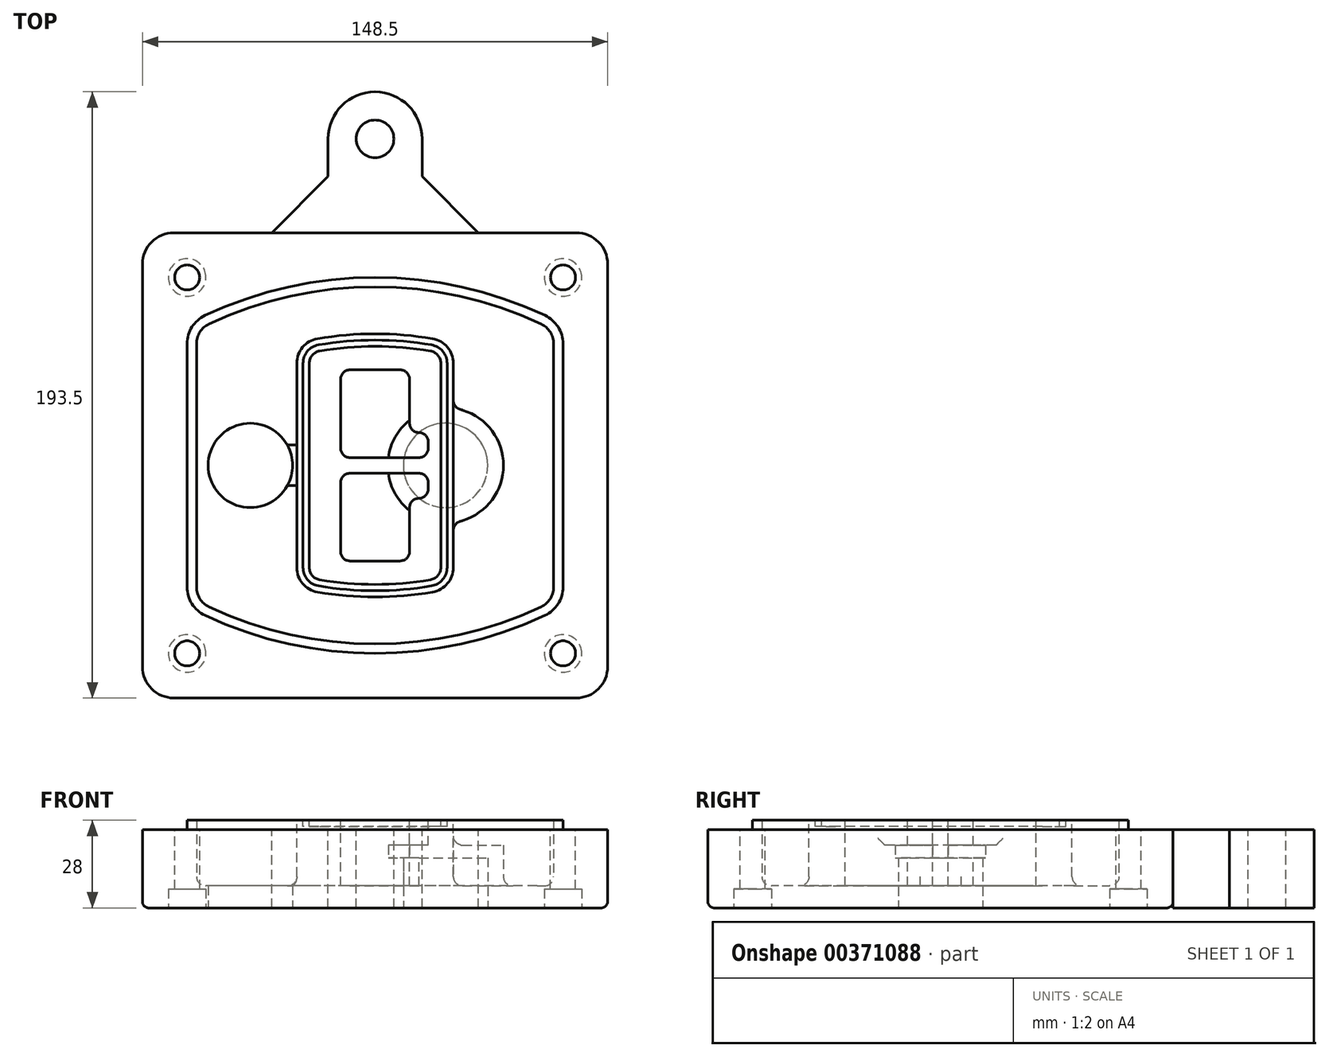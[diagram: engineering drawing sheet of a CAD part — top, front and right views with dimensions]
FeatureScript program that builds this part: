
annotation { "Feature Type Name" : "Feature", "Feature Type Description" : "" }
export const myFeature = defineFeature(function(context is Context, id is Id, definition is map)
    precondition{}
    {
        {
            var Q0;
            Q0=qCreatedBy(makeId("Top.planeOp"),FACE);
            var sketch = newSketch(context, id + "F0", { "sketchPlane" : qUnion([Q0])});
            skPoint(sketch, "E0.rect.middle", {"position": v(0, 0) * mm});
            skLineSegment(sketch, "E1.bottom", {"start": v(-64.25, -74.25) * mm, "end": v(64.25, -74.25) * mm});
            skLineSegment(sketch, "E1.top", {"start": v(-64.25, 74.25) * mm, "end": v(64.25, 74.25) * mm});
            skLineSegment(sketch, "E1.left", {"start": v(-74.25, -64.25) * mm, "end": v(-74.25, 64.25) * mm});
            skLineSegment(sketch, "E1.right", {"start": v(74.25, -64.25) * mm, "end": v(74.25, 64.25) * mm});
            skLineSegment(sketch, "E2", {"start": v(-74.25, 74.25) * mm, "end": v(74.25, -74.25) * mm, "construction": true});
            skLineSegment(sketch, "E3", {"start": v(74.25, 74.25) * mm, "end": v(-74.25, -74.25) * mm, "construction": true});
            skCircle(sketch, "E4", {"center": v(-60, 60) * mm, "radius": 4 * mm});
            skCircle(sketch, "E5", {"center": v(60, 60) * mm, "radius": 4 * mm});
            skCircle(sketch, "E6", {"center": v(60, -60) * mm, "radius": 4 * mm});
            skCircle(sketch, "E7", {"center": v(-60, -60) * mm, "radius": 4 * mm});
            skLineSegment(sketch, "E8", {"start": v(-60, 60) * mm, "end": v(60, 60) * mm, "construction": true});
            skLineSegment(sketch, "E9", {"start": v(60, 60) * mm, "end": v(60, -60) * mm, "construction": true});
            skLineSegment(sketch, "E10", {"start": v(60, -60) * mm, "end": v(-60, -60) * mm, "construction": true});
            skLineSegment(sketch, "E11", {"start": v(-60, -60) * mm, "end": v(-60, 60) * mm, "construction": true});
            skLineSegment(sketch, "E12", {"start": v(-60, 38.83) * mm, "end": v(-60, -38.83) * mm});
            skLineSegment(sketch, "E13", {"start": v(60, 38.83) * mm, "end": v(60, -38.83) * mm});
            skArc(sketch, "E14", {"start": v(54.26, 47.88) * mm, "mid": v(0, 60) * mm, "end": v(-54.26, 47.88) * mm});
            skArc(sketch, "E15", {"start": v(-54.26, -47.88) * mm, "mid": v(0, -60) * mm, "end": v(54.26, -47.88) * mm});
            skLineSegment(sketch, "E16", {"start": v(-60, 0) * mm, "end": v(60, 0) * mm, "construction": true});
            skPoint(sketch, "E17.visualSharp", {"position": v(-60, -45) * mm});
            skArc(sketch, "E17.filletArc", {"start": v(-60, -38.83) * mm, "mid": v(-58.44, -44.2) * mm, "end": v(-54.26, -47.88) * mm});
            skPoint(sketch, "E18.visualSharp", {"position": v(-60, 45) * mm});
            skArc(sketch, "E18.filletArc", {"start": v(-54.26, 47.88) * mm, "mid": v(-58.44, 44.2) * mm, "end": v(-60, 38.83) * mm});
            skPoint(sketch, "E19.visualSharp", {"position": v(60, 45) * mm});
            skArc(sketch, "E19.filletArc", {"start": v(60, 38.83) * mm, "mid": v(58.44, 44.2) * mm, "end": v(54.26, 47.88) * mm});
            skPoint(sketch, "E20.visualSharp", {"position": v(60, -45) * mm});
            skArc(sketch, "E20.filletArc", {"start": v(54.26, -47.88) * mm, "mid": v(58.44, -44.2) * mm, "end": v(60, -38.83) * mm});
            skPoint(sketch, "E21.visualSharp", {"position": v(-74.25, 74.25) * mm});
            skArc(sketch, "E21.filletArc", {"start": v(-64.25, 74.25) * mm, "mid": v(-71.32, 71.32) * mm, "end": v(-74.25, 64.25) * mm});
            skPoint(sketch, "E22.visualSharp", {"position": v(74.25, 74.25) * mm});
            skArc(sketch, "E22.filletArc", {"start": v(74.25, 64.25) * mm, "mid": v(71.32, 71.32) * mm, "end": v(64.25, 74.25) * mm});
            skPoint(sketch, "E23.visualSharp", {"position": v(74.25, -74.25) * mm});
            skArc(sketch, "E23.filletArc", {"start": v(64.25, -74.25) * mm, "mid": v(71.32, -71.32) * mm, "end": v(74.25, -64.25) * mm});
            skPoint(sketch, "E24.visualSharp", {"position": v(-74.25, -74.25) * mm});
            skArc(sketch, "E24.filletArc", {"start": v(-74.25, -64.25) * mm, "mid": v(-71.32, -71.32) * mm, "end": v(-64.25, -74.25) * mm});
            skArc(sketch, "E25.0", {"start": v(57, 38.83) * mm, "mid": v(55.9, 42.58) * mm, "end": v(52.98, 45.17) * mm});
            skLineSegment(sketch, "E25.1", {"start": v(57, 38.83) * mm, "end": v(57, -38.83) * mm});
            skArc(sketch, "E25.2", {"start": v(52.98, -45.17) * mm, "mid": v(55.9, -42.58) * mm, "end": v(57, -38.83) * mm});
            skArc(sketch, "E25.3", {"start": v(-52.98, -45.17) * mm, "mid": v(0, -57) * mm, "end": v(52.98, -45.17) * mm});
            skArc(sketch, "E25.4", {"start": v(-57, -38.83) * mm, "mid": v(-55.9, -42.58) * mm, "end": v(-52.98, -45.17) * mm});
            skArc(sketch, "E25.5", {"start": v(52.98, 45.17) * mm, "mid": v(0, 57) * mm, "end": v(-52.98, 45.17) * mm});
            skLineSegment(sketch, "E25.6", {"start": v(-57, 38.83) * mm, "end": v(-57, -38.83) * mm});
            skArc(sketch, "E25.7", {"start": v(-52.98, 45.17) * mm, "mid": v(-55.9, 42.58) * mm, "end": v(-57, 38.83) * mm});
            skArc(sketch, "E26.0", {"start": v(-55.96, 51.5) * mm, "mid": v(-61.82, 46.33) * mm, "end": v(-64, 38.83) * mm});
            skArc(sketch, "E26.1", {"start": v(55.96, 51.5) * mm, "mid": v(0, 64) * mm, "end": v(-55.96, 51.5) * mm});
            skArc(sketch, "E26.2", {"start": v(64, 38.83) * mm, "mid": v(61.82, 46.33) * mm, "end": v(55.96, 51.5) * mm});
            skLineSegment(sketch, "E26.3", {"start": v(64, 38.83) * mm, "end": v(64, -38.83) * mm});
            skArc(sketch, "E26.4", {"start": v(55.96, -51.5) * mm, "mid": v(61.82, -46.33) * mm, "end": v(64, -38.83) * mm});
            skLineSegment(sketch, "E26.5", {"start": v(-64, 38.83) * mm, "end": v(-64, -38.83) * mm});
            skArc(sketch, "E26.6", {"start": v(-55.96, -51.5) * mm, "mid": v(0, -64) * mm, "end": v(55.96, -51.5) * mm});
            skArc(sketch, "E26.7", {"start": v(-64, -38.83) * mm, "mid": v(-61.82, -46.33) * mm, "end": v(-55.96, -51.5) * mm});
            skSolve(sketch);
        }
        {
            var Q0;
            Q0=makeQuery(id+"F0.imprint","IMPRINT",FACE,{"disambiguationData":[TD([[makeQuery(id+"F0.imprint","IMPRINT",EDGE,{"derivedFrom":sQuery(id+"F0.wireOp",EDGE,"E1.bottom")}),1.0]])]});
            var Q1;
            Q1=makeQuery(id+"F0.imprint","IMPRINT",FACE,{"disambiguationData":[TD([[makeQuery(id+"F0.imprint","IMPRINT",EDGE,{"derivedFrom":sQuery(id+"F0.wireOp",EDGE,"E12")}),1.0]])]});
            var Q2;
            Q2=makeQuery(id+"F0.imprint","IMPRINT",FACE,{"disambiguationData":[TD([[makeQuery(id+"F0.imprint","IMPRINT",EDGE,{"derivedFrom":sQuery(id+"F0.wireOp",EDGE,"E25.0")}),1.0]])]});
            var Q3;
            Q3=makeQuery(id+"F0.imprint","IMPRINT",FACE,{"disambiguationData":[TD([[makeQuery(id+"F0.imprint","IMPRINT",EDGE,{"derivedFrom":sQuery(id+"F0.wireOp",EDGE,"E12")}),-1.0]])]});
            extrude(context, id + "F1", {"entities" : qUnion([Q0, Q1, Q2, Q3]), "oppositeDirection" : true, "depth" : 25 * mm});
        }
        {
            var Q0;
            Q0=makeQuery(id+"F0.imprint","IMPRINT",FACE,{"disambiguationData":[TD([[makeQuery(id+"F0.imprint","IMPRINT",EDGE,{"derivedFrom":sQuery(id+"F0.wireOp",EDGE,"E12")}),1.0]])]});
            extrude(context, id + "F2", {"entities" : qUnion([Q0]), "operationType" : NewBodyOperationType.ADD, "depth" : 3 * mm});
        }
        {
            var Q0;
            Q0=makeQuery(id+"F0.imprint","IMPRINT",FACE,{"disambiguationData":[TD([[makeQuery(id+"F0.imprint","IMPRINT",EDGE,{"derivedFrom":sQuery(id+"F0.wireOp",EDGE,"E25.0")}),1.0]])]});
            extrude(context, id + "F3", {"entities" : qUnion([Q0]), "operationType" : NewBodyOperationType.REMOVE, "oppositeDirection" : true, "depth" : 18 * mm});
        }
        {
            var Q0;
            Q0=makeQuery(id+"F2.opExtrude","CAP_FACE",FACE,{"disambiguationData":[OSD([sQuery(id+"F0.wireOp",EDGE,"E12"),sQuery(id+"F0.wireOp",EDGE,"E13"),sQuery(id+"F0.wireOp",EDGE,"E14"),sQuery(id+"F0.wireOp",EDGE,"E15"),sQuery(id+"F0.wireOp",EDGE,"E17.filletArc"),sQuery(id+"F0.wireOp",EDGE,"E18.filletArc"),sQuery(id+"F0.wireOp",EDGE,"E19.filletArc"),sQuery(id+"F0.wireOp",EDGE,"E20.filletArc"),sQuery(id+"F0.wireOp",EDGE,"E25.0"),sQuery(id+"F0.wireOp",EDGE,"E25.1"),sQuery(id+"F0.wireOp",EDGE,"E25.2"),sQuery(id+"F0.wireOp",EDGE,"E25.3"),sQuery(id+"F0.wireOp",EDGE,"E25.4"),sQuery(id+"F0.wireOp",EDGE,"E25.5"),sQuery(id+"F0.wireOp",EDGE,"E25.6"),sQuery(id+"F0.wireOp",EDGE,"E25.7")])],"isStart":false});
            var sketch = newSketch(context, id + "F4", { "sketchPlane" : qUnion([Q0])});
            skArc(sketch, "E27.0", {"start": v(-18.34, -40.45) * mm, "mid": v(0, -42) * mm, "end": v(18.34, -40.45) * mm});
            skArc(sketch, "E28.0", {"start": v(18.34, 40.45) * mm, "mid": v(0, 42) * mm, "end": v(-18.34, 40.45) * mm});
            skLineSegment(sketch, "E29", {"start": v(-25, 32.57) * mm, "end": v(-25, -32.57) * mm});
            skLineSegment(sketch, "E30", {"start": v(25, 32.57) * mm, "end": v(25, -32.57) * mm});
            skLineSegment(sketch, "E31", {"start": v(-25, 39.1) * mm, "end": v(25, 39.1) * mm, "construction": true});
            skLineSegment(sketch, "E32", {"start": v(-25, -39.1) * mm, "end": v(25, -39.1) * mm, "construction": true});
            skPoint(sketch, "E33.visualSharp", {"position": v(-25, 39.1) * mm});
            skArc(sketch, "E33.filletArc", {"start": v(-18.34, 40.45) * mm, "mid": v(-23.11, 37.73) * mm, "end": v(-25, 32.57) * mm});
            skPoint(sketch, "E34.visualSharp", {"position": v(25, 39.1) * mm});
            skArc(sketch, "E34.filletArc", {"start": v(25, 32.57) * mm, "mid": v(23.11, 37.73) * mm, "end": v(18.34, 40.45) * mm});
            skPoint(sketch, "E35.visualSharp", {"position": v(25, -39.1) * mm});
            skArc(sketch, "E35.filletArc", {"start": v(18.34, -40.45) * mm, "mid": v(23.11, -37.73) * mm, "end": v(25, -32.57) * mm});
            skPoint(sketch, "E36.visualSharp", {"position": v(-25, -39.1) * mm});
            skArc(sketch, "E36.filletArc", {"start": v(-25, -32.57) * mm, "mid": v(-23.11, -37.73) * mm, "end": v(-18.34, -40.45) * mm});
            skArc(sketch, "E37.0", {"start": v(52.98, 45.17) * mm, "mid": v(0, 57) * mm, "end": v(-52.98, 45.17) * mm});
            skArc(sketch, "E37.1", {"start": v(-52.98, 45.17) * mm, "mid": v(-55.9, 42.58) * mm, "end": v(-57, 38.83) * mm});
            skLineSegment(sketch, "E37.2", {"start": v(-57, 38.83) * mm, "end": v(-57, -38.83) * mm});
            skArc(sketch, "E37.3", {"start": v(-57, -38.83) * mm, "mid": v(-55.9, -42.58) * mm, "end": v(-52.98, -45.17) * mm});
            skArc(sketch, "E37.4", {"start": v(-52.98, -45.17) * mm, "mid": v(0, -57) * mm, "end": v(52.98, -45.17) * mm});
            skArc(sketch, "E37.5", {"start": v(52.98, -45.17) * mm, "mid": v(55.9, -42.58) * mm, "end": v(57, -38.83) * mm});
            skLineSegment(sketch, "E37.6", {"start": v(57, 38.83) * mm, "end": v(57, -38.83) * mm});
            skArc(sketch, "E37.7", {"start": v(57, 38.83) * mm, "mid": v(55.9, 42.58) * mm, "end": v(52.98, 45.17) * mm});
            skLineSegment(sketch, "E38.0", {"start": v(23, 32.57) * mm, "end": v(23, -32.57) * mm});
            skArc(sketch, "E38.1", {"start": v(18, -38.48) * mm, "mid": v(21.58, -36.44) * mm, "end": v(23, -32.57) * mm});
            skArc(sketch, "E38.2", {"start": v(-18, -38.48) * mm, "mid": v(0, -40) * mm, "end": v(18, -38.48) * mm});
            skArc(sketch, "E38.3", {"start": v(-23, -32.57) * mm, "mid": v(-21.58, -36.44) * mm, "end": v(-18, -38.48) * mm});
            skLineSegment(sketch, "E38.4", {"start": v(-23, 32.57) * mm, "end": v(-23, -32.57) * mm});
            skArc(sketch, "E38.5", {"start": v(23, 32.57) * mm, "mid": v(21.58, 36.44) * mm, "end": v(18, 38.48) * mm});
            skArc(sketch, "E38.6", {"start": v(-18, 38.48) * mm, "mid": v(-21.58, 36.44) * mm, "end": v(-23, 32.57) * mm});
            skArc(sketch, "E38.7", {"start": v(18, 38.48) * mm, "mid": v(0, 40) * mm, "end": v(-18, 38.48) * mm});
            skArc(sketch, "E39.0", {"start": v(21, 32.57) * mm, "mid": v(20.06, 35.15) * mm, "end": v(17.67, 36.5) * mm});
            skLineSegment(sketch, "E39.1", {"start": v(21, 32.57) * mm, "end": v(21, -32.57) * mm});
            skArc(sketch, "E39.2", {"start": v(17.67, -36.5) * mm, "mid": v(20.06, -35.15) * mm, "end": v(21, -32.57) * mm});
            skArc(sketch, "E39.3", {"start": v(-17.67, -36.5) * mm, "mid": v(0, -38) * mm, "end": v(17.67, -36.5) * mm});
            skArc(sketch, "E39.4", {"start": v(-21, -32.57) * mm, "mid": v(-20.06, -35.15) * mm, "end": v(-17.67, -36.5) * mm});
            skArc(sketch, "E39.5", {"start": v(17.67, 36.5) * mm, "mid": v(0, 38) * mm, "end": v(-17.67, 36.5) * mm});
            skLineSegment(sketch, "E39.6", {"start": v(-21, 32.57) * mm, "end": v(-21, -32.57) * mm});
            skArc(sketch, "E39.7", {"start": v(-17.67, 36.5) * mm, "mid": v(-20.06, 35.15) * mm, "end": v(-21, 32.57) * mm});
            skLineSegment(sketch, "E40", {"start": v(-25, 0) * mm, "end": v(25, 0) * mm, "construction": true});
            skLineSegment(sketch, "E41", {"start": v(-11, 5.5) * mm, "end": v(-11, 27.5) * mm});
            skLineSegment(sketch, "E42", {"start": v(-8, 30.5) * mm, "end": v(8, 30.5) * mm});
            skLineSegment(sketch, "E43", {"start": v(11, 27.5) * mm, "end": v(11, 13.5) * mm});
            skLineSegment(sketch, "E44", {"start": v(14, 10.5) * mm, "end": v(14, 10.5) * mm});
            skLineSegment(sketch, "E45", {"start": v(17, 7.5) * mm, "end": v(17, 5.5) * mm});
            skLineSegment(sketch, "E46", {"start": v(14, 2.5) * mm, "end": v(-8, 2.5) * mm});
            skPoint(sketch, "E47.visualSharp", {"position": v(-11, 30.5) * mm});
            skArc(sketch, "E47.filletArc", {"start": v(-8, 30.5) * mm, "mid": v(-10.12, 29.62) * mm, "end": v(-11, 27.5) * mm});
            skPoint(sketch, "E48.visualSharp", {"position": v(11, 30.5) * mm});
            skArc(sketch, "E48.filletArc", {"start": v(11, 27.5) * mm, "mid": v(10.12, 29.62) * mm, "end": v(8, 30.5) * mm});
            skPoint(sketch, "E49.visualSharp", {"position": v(11, 10.5) * mm});
            skArc(sketch, "E49.filletArc", {"start": v(11, 13.5) * mm, "mid": v(11.88, 11.38) * mm, "end": v(14, 10.5) * mm});
            skPoint(sketch, "E50.visualSharp", {"position": v(17, 10.5) * mm});
            skArc(sketch, "E50.filletArc", {"start": v(17, 7.5) * mm, "mid": v(16.12, 9.62) * mm, "end": v(14, 10.5) * mm});
            skPoint(sketch, "E51.visualSharp", {"position": v(17, 2.5) * mm});
            skArc(sketch, "E51.filletArc", {"start": v(14, 2.5) * mm, "mid": v(16.12, 3.38) * mm, "end": v(17, 5.5) * mm});
            skPoint(sketch, "E52.visualSharp", {"position": v(-11, 2.5) * mm});
            skArc(sketch, "E52.filletArc", {"start": v(-11, 5.5) * mm, "mid": v(-10.12, 3.38) * mm, "end": v(-8, 2.5) * mm});
            skLineSegment(sketch, "E53.0.MirrorCS", {"start": v(14, -2.5) * mm, "end": v(-8, -2.5) * mm});
            skArc(sketch, "E54.0.MirrorCS", {"start": v(-11, -5.5) * mm, "mid": v(-10.12, -3.38) * mm, "end": v(-8, -2.5) * mm});
            skLineSegment(sketch, "E55.0.MirrorCS", {"start": v(-11, -5.5) * mm, "end": v(-11, -27.5) * mm});
            skArc(sketch, "E56.0.MirrorCS", {"start": v(-8, -30.5) * mm, "mid": v(-10.12, -29.62) * mm, "end": v(-11, -27.5) * mm});
            skLineSegment(sketch, "E57.0.MirrorCS", {"start": v(-8, -30.5) * mm, "end": v(8, -30.5) * mm});
            skArc(sketch, "E58.0.MirrorCS", {"start": v(11, -27.5) * mm, "mid": v(10.12, -29.62) * mm, "end": v(8, -30.5) * mm});
            skLineSegment(sketch, "E59.0.MirrorCS", {"start": v(11, -27.5) * mm, "end": v(11, -13.5) * mm});
            skArc(sketch, "E60.0.MirrorCS", {"start": v(11, -13.5) * mm, "mid": v(11.88, -11.38) * mm, "end": v(14, -10.5) * mm});
            skArc(sketch, "E61.0.MirrorCS", {"start": v(17, -7.5) * mm, "mid": v(16.12, -9.62) * mm, "end": v(14, -10.5) * mm});
            skLineSegment(sketch, "E62.0.MirrorCS", {"start": v(17, -7.5) * mm, "end": v(17, -5.5) * mm});
            skArc(sketch, "E63.0.MirrorCS", {"start": v(14, -2.5) * mm, "mid": v(16.12, -3.38) * mm, "end": v(17, -5.5) * mm});
            skSolve(sketch);
        }
        {
            var Q0;
            Q0=makeQuery(id+"F4.imprint","IMPRINT",FACE,{"disambiguationData":[TD([[makeQuery(id+"F4.imprint","IMPRINT",EDGE,{"derivedFrom":sQuery(id+"F4.wireOp",EDGE,"E27.0")}),1.0]])]});
            var Q1;
            Q1=makeQuery(id+"F4.imprint","IMPRINT",FACE,{"disambiguationData":[TD([[makeQuery(id+"F4.imprint","IMPRINT",EDGE,{"derivedFrom":sQuery(id+"F4.wireOp",EDGE,"E38.0")}),-1.0]])]});
            var Q2;
            Q2=makeQuery(id+"F4.imprint","IMPRINT",FACE,{"disambiguationData":[TD([[makeQuery(id+"F4.imprint","IMPRINT",EDGE,{"derivedFrom":sQuery(id+"F4.wireOp",EDGE,"E39.0")}),1.0]])]});
            extrude(context, id + "F5", {"entities" : qUnion([Q0, Q1, Q2]), "operationType" : NewBodyOperationType.ADD, "endBound" : BoundingType.UP_TO_NEXT, "oppositeDirection" : true, "depth" : 25 * mm});
        }
        {
            var Q0;
            Q0=makeQuery(id+"F4.imprint","IMPRINT",FACE,{"disambiguationData":[TD([[makeQuery(id+"F4.imprint","IMPRINT",EDGE,{"derivedFrom":sQuery(id+"F4.wireOp",EDGE,"E38.0")}),-1.0]])]});
            extrude(context, id + "F6", {"entities" : qUnion([Q0]), "operationType" : NewBodyOperationType.REMOVE, "oppositeDirection" : true, "depth" : 2 * mm});
        }
        {
            var Q0;
            Q0=makeQuery(id+"F1.opExtrude","CAP_FACE",FACE,{"disambiguationData":[OSD([sQuery(id+"F0.wireOp",EDGE,"E1.bottom"),sQuery(id+"F0.wireOp",EDGE,"E1.top"),sQuery(id+"F0.wireOp",EDGE,"E1.left"),sQuery(id+"F0.wireOp",EDGE,"E1.right"),sQuery(id+"F0.wireOp",EDGE,"E4"),sQuery(id+"F0.wireOp",EDGE,"E5"),sQuery(id+"F0.wireOp",EDGE,"E6"),sQuery(id+"F0.wireOp",EDGE,"E7"),sQuery(id+"F0.wireOp",EDGE,"E21.filletArc"),sQuery(id+"F0.wireOp",EDGE,"E22.filletArc"),sQuery(id+"F0.wireOp",EDGE,"E23.filletArc"),sQuery(id+"F0.wireOp",EDGE,"E24.filletArc")])],"isStart":false});
            var sketch = newSketch(context, id + "F7", { "sketchPlane" : qUnion([Q0])});
            skCircle(sketch, "E64", {"center": v(22.5, 0) * mm, "radius": 13.47 * mm});
            skCircle(sketch, "E65", {"center": v(-39.81, 0) * mm, "radius": 13.47 * mm});
            skLineSegment(sketch, "E66", {"start": v(74.25, 0) * mm, "end": v(-74.25, 0) * mm});
            skCircle(sketch, "E67", {"center": v(22.5, 0) * mm, "radius": 18.47 * mm});
            skCircle(sketch, "E68", {"center": v(60, -60) * mm, "radius": 6 * mm});
            skCircle(sketch, "E69", {"center": v(-60, -60) * mm, "radius": 6 * mm});
            skCircle(sketch, "E70", {"center": v(-60, 60) * mm, "radius": 6 * mm});
            skCircle(sketch, "E71", {"center": v(60, 60) * mm, "radius": 6 * mm});
            skSolve(sketch);
        }
        {
            var Q0;
            {var subQ1=sQuery(id+"F7.wireOp",EDGE,"E66");var subQ4=sQuery(id+"F7.wireOp",EDGE,"E64");var subQ6=makeQuery(id+"F7.imprint","INTERSECT",VERTEX,{"disambiguationData":[OD(0.0)],"derivedFrom":[subQ4,subQ1]});Q0=makeQuery(id+"F7.imprint","IMPRINT",FACE,{"disambiguationData":[TD([[makeQuery(id+"F7.imprint","IMPRINT",EDGE,{"disambiguationData":[TD([[subQ6,-1.0]])],"derivedFrom":subQ4}),-1.0]])]});}
            var Q1;
            {var subQ0=sQuery(id+"F7.wireOp",EDGE,"E66");var subQ1=sQuery(id+"F7.wireOp",EDGE,"E64");var subQ3=makeQuery(id+"F7.imprint","INTERSECT",VERTEX,{"disambiguationData":[OD(0.0)],"derivedFrom":[subQ1,subQ0]});Q1=makeQuery(id+"F7.imprint","IMPRINT",FACE,{"disambiguationData":[TD([[makeQuery(id+"F7.imprint","IMPRINT",EDGE,{"disambiguationData":[TD([[subQ3,-1.0]])],"derivedFrom":subQ1}),1.0]])]});}
            var Q2;
            {var subQ0=sQuery(id+"F7.wireOp",EDGE,"E66");var subQ1=sQuery(id+"F7.wireOp",EDGE,"E64");var subQ3=makeQuery(id+"F7.imprint","INTERSECT",VERTEX,{"disambiguationData":[OD(0.0)],"derivedFrom":[subQ1,subQ0]});Q2=makeQuery(id+"F7.imprint","IMPRINT",FACE,{"disambiguationData":[TD([[makeQuery(id+"F7.imprint","IMPRINT",EDGE,{"disambiguationData":[TD([[subQ3,1.0]])],"derivedFrom":subQ1}),1.0]])]});}
            var Q3;
            {var subQ1=sQuery(id+"F7.wireOp",EDGE,"E66");var subQ4=sQuery(id+"F7.wireOp",EDGE,"E64");var subQ6=makeQuery(id+"F7.imprint","INTERSECT",VERTEX,{"disambiguationData":[OD(0.0)],"derivedFrom":[subQ4,subQ1]});Q3=makeQuery(id+"F7.imprint","IMPRINT",FACE,{"disambiguationData":[TD([[makeQuery(id+"F7.imprint","IMPRINT",EDGE,{"disambiguationData":[TD([[subQ6,1.0]])],"derivedFrom":subQ4}),-1.0]])]});}
            extrude(context, id + "F8", {"entities" : qUnion([Q0, Q1, Q2, Q3]), "operationType" : NewBodyOperationType.ADD, "oppositeDirection" : true, "depth" : 20 * mm});
        }
        {
            var Q0;
            {var subQ0=sQuery(id+"F7.wireOp",EDGE,"E66");var subQ1=sQuery(id+"F7.wireOp",EDGE,"E64");var subQ3=makeQuery(id+"F7.imprint","INTERSECT",VERTEX,{"disambiguationData":[OD(0.0)],"derivedFrom":[subQ1,subQ0]});Q0=makeQuery(id+"F7.imprint","IMPRINT",FACE,{"disambiguationData":[TD([[makeQuery(id+"F7.imprint","IMPRINT",EDGE,{"disambiguationData":[TD([[subQ3,-1.0]])],"derivedFrom":subQ1}),1.0]])]});}
            var Q1;
            {var subQ0=sQuery(id+"F7.wireOp",EDGE,"E66");var subQ1=sQuery(id+"F7.wireOp",EDGE,"E64");var subQ3=makeQuery(id+"F7.imprint","INTERSECT",VERTEX,{"disambiguationData":[OD(0.0)],"derivedFrom":[subQ1,subQ0]});Q1=makeQuery(id+"F7.imprint","IMPRINT",FACE,{"disambiguationData":[TD([[makeQuery(id+"F7.imprint","IMPRINT",EDGE,{"disambiguationData":[TD([[subQ3,1.0]])],"derivedFrom":subQ1}),1.0]])]});}
            extrude(context, id + "F9", {"entities" : qUnion([Q0, Q1]), "operationType" : NewBodyOperationType.REMOVE, "oppositeDirection" : true, "depth" : 16 * mm});
        }
        {
            var Q0;
            {var subQ0=sQuery(id+"F7.wireOp",EDGE,"E66");var subQ1=sQuery(id+"F7.wireOp",EDGE,"E65");var subQ3=makeQuery(id+"F7.imprint","INTERSECT",VERTEX,{"disambiguationData":[OD(0.0)],"derivedFrom":[subQ1,subQ0]});Q0=makeQuery(id+"F7.imprint","IMPRINT",FACE,{"disambiguationData":[TD([[makeQuery(id+"F7.imprint","IMPRINT",EDGE,{"disambiguationData":[TD([[subQ3,-1.0]])],"derivedFrom":subQ1}),1.0]])]});}
            var Q1;
            {var subQ0=sQuery(id+"F7.wireOp",EDGE,"E66");var subQ1=sQuery(id+"F7.wireOp",EDGE,"E65");var subQ3=makeQuery(id+"F7.imprint","INTERSECT",VERTEX,{"disambiguationData":[OD(0.0)],"derivedFrom":[subQ1,subQ0]});Q1=makeQuery(id+"F7.imprint","IMPRINT",FACE,{"disambiguationData":[TD([[makeQuery(id+"F7.imprint","IMPRINT",EDGE,{"disambiguationData":[TD([[subQ3,1.0]])],"derivedFrom":subQ1}),1.0]])]});}
            extrude(context, id + "F10", {"entities" : qUnion([Q0, Q1]), "operationType" : NewBodyOperationType.REMOVE, "oppositeDirection" : true, "depth" : 25 * mm});
        }
        {
            var Q0;
            Q0=makeQuery(id+"F7.imprint","IMPRINT",FACE,{"disambiguationData":[TD([[makeQuery(id+"F7.imprint","IMPRINT",EDGE,{"derivedFrom":sQuery(id+"F7.wireOp",EDGE,"E68")}),1.0]])]});
            var Q1;
            Q1=makeQuery(id+"F7.imprint","IMPRINT",FACE,{"disambiguationData":[TD([[makeQuery(id+"F7.imprint","IMPRINT",EDGE,{"derivedFrom":makeQuery(id+"F1.opExtrude","CAP_EDGE",EDGE,{"disambiguationData":[OSD([sQuery(id+"F0.wireOp",EDGE,"E5")])],"isStart":false})}),-1.0]])]});
            var Q2;
            Q2=makeQuery(id+"F7.imprint","IMPRINT",FACE,{"disambiguationData":[TD([[makeQuery(id+"F7.imprint","IMPRINT",EDGE,{"derivedFrom":sQuery(id+"F7.wireOp",EDGE,"E69")}),1.0]])]});
            var Q3;
            Q3=makeQuery(id+"F7.imprint","IMPRINT",FACE,{"disambiguationData":[TD([[makeQuery(id+"F7.imprint","IMPRINT",EDGE,{"derivedFrom":makeQuery(id+"F1.opExtrude","CAP_EDGE",EDGE,{"disambiguationData":[OSD([sQuery(id+"F0.wireOp",EDGE,"E4")])],"isStart":false})}),-1.0]])]});
            var Q4;
            Q4=makeQuery(id+"F7.imprint","IMPRINT",FACE,{"disambiguationData":[TD([[makeQuery(id+"F7.imprint","IMPRINT",EDGE,{"derivedFrom":sQuery(id+"F7.wireOp",EDGE,"E70")}),1.0]])]});
            var Q5;
            Q5=makeQuery(id+"F7.imprint","IMPRINT",FACE,{"disambiguationData":[TD([[makeQuery(id+"F7.imprint","IMPRINT",EDGE,{"derivedFrom":makeQuery(id+"F1.opExtrude","CAP_EDGE",EDGE,{"disambiguationData":[OSD([sQuery(id+"F0.wireOp",EDGE,"E7")])],"isStart":false})}),-1.0]])]});
            var Q6;
            Q6=makeQuery(id+"F7.imprint","IMPRINT",FACE,{"disambiguationData":[TD([[makeQuery(id+"F7.imprint","IMPRINT",EDGE,{"derivedFrom":sQuery(id+"F7.wireOp",EDGE,"E71")}),1.0]])]});
            var Q7;
            Q7=makeQuery(id+"F7.imprint","IMPRINT",FACE,{"disambiguationData":[TD([[makeQuery(id+"F7.imprint","IMPRINT",EDGE,{"derivedFrom":makeQuery(id+"F1.opExtrude","CAP_EDGE",EDGE,{"disambiguationData":[OSD([sQuery(id+"F0.wireOp",EDGE,"E6")])],"isStart":false})}),-1.0]])]});
            extrude(context, id + "F11", {"entities" : qUnion([Q0, Q1, Q2, Q3, Q4, Q5, Q6, Q7]), "operationType" : NewBodyOperationType.REMOVE, "oppositeDirection" : true, "depth" : 6 * mm});
        }
        {
            var Q0;
            Q0=makeQuery(id+"F9.boolean.opBoolean","COPY",FACE,{"derivedFrom":makeQuery(id+"F9.opExtrude","CAP_FACE",FACE,{"disambiguationData":[OSD([sQuery(id+"F7.wireOp",EDGE,"E64")])],"isStart":false})});
            var sketch = newSketch(context, id + "F12", { "sketchPlane" : qUnion([Q0])});
            skArc(sketch, "E72.0", {"start": v(11, 14.45) * mm, "mid": v(6.45, 9.13) * mm, "end": v(4.2, 2.5) * mm});
            skArc(sketch, "E72.1", {"start": v(4.2, -2.5) * mm, "mid": v(6.45, -9.13) * mm, "end": v(11, -14.45) * mm});
            skLineSegment(sketch, "E73", {"start": v(4.2, -2.5) * mm, "end": v(14, -2.5) * mm});
            skLineSegment(sketch, "E74.0", {"start": v(14, 2.5) * mm, "end": v(4.2, 2.5) * mm});
            skArc(sketch, "E74.1", {"start": v(14, 2.5) * mm, "mid": v(16.12, 3.38) * mm, "end": v(17, 5.5) * mm});
            skLineSegment(sketch, "E74.2", {"start": v(17, 7.5) * mm, "end": v(17, 5.5) * mm});
            skArc(sketch, "E74.3", {"start": v(17, 7.5) * mm, "mid": v(16.12, 9.62) * mm, "end": v(14, 10.5) * mm});
            skArc(sketch, "E74.4", {"start": v(11, 13.5) * mm, "mid": v(11.88, 11.38) * mm, "end": v(14, 10.5) * mm});
            skLineSegment(sketch, "E74.5", {"start": v(11, 14.45) * mm, "end": v(11, 13.5) * mm});
            skLineSegment(sketch, "E74.7", {"start": v(14, -2.5) * mm, "end": v(4.2, -2.5) * mm});
            skArc(sketch, "E74.8", {"start": v(14, -2.5) * mm, "mid": v(16.12, -3.38) * mm, "end": v(17, -5.5) * mm});
            skLineSegment(sketch, "E74.9", {"start": v(17, -7.5) * mm, "end": v(17, -5.5) * mm});
            skArc(sketch, "E74.10", {"start": v(17, -7.5) * mm, "mid": v(16.12, -9.62) * mm, "end": v(14, -10.5) * mm});
            skArc(sketch, "E74.11", {"start": v(11, -13.5) * mm, "mid": v(11.88, -11.38) * mm, "end": v(14, -10.5) * mm});
            skLineSegment(sketch, "E74.12", {"start": v(11, -14.45) * mm, "end": v(11, -13.5) * mm});
            skPoint(sketch, "E75.orphan", {"position": v(11, -27.5) * mm});
            skPoint(sketch, "E76.orphan", {"position": v(-8, -2.5) * mm});
            skPoint(sketch, "E77.orphan", {"position": v(-8, 2.5) * mm});
            skPoint(sketch, "E78.orphan", {"position": v(11, 27.5) * mm});
            skSolve(sketch);
        }
        {
            var Q0;
            {var subQ7=sQuery(id+"F12.wireOp",EDGE,"E72.0");var subQ14=sQuery(id+"F12.wireOp",EDGE,"E72.1");var subQ16=sQuery(id+"F12.wireOp",EDGE,"E74.1");var subQ18=sQuery(id+"F12.wireOp",EDGE,"E74.8");Q0=qUnion([makeQuery(id+"F12.imprint","IMPRINT",FACE,{"disambiguationData":[TD([[makeQuery(id+"F12.imprint","IMPRINT",EDGE,{"derivedFrom":subQ7}),1.0]])]}),makeQuery(id+"F12.imprint","IMPRINT",FACE,{"disambiguationData":[TD([[makeQuery(id+"F12.imprint","IMPRINT",EDGE,{"derivedFrom":subQ14}),1.0]])]}),makeQuery(id+"F12.imprint","IMPRINT",FACE,{"disambiguationData":[TD([[makeQuery(id+"F12.imprint","IMPRINT",EDGE,{"derivedFrom":subQ16}),1.0]])]}),makeQuery(id+"F12.imprint","IMPRINT",FACE,{"disambiguationData":[TD([[makeQuery(id+"F12.imprint","IMPRINT",EDGE,{"derivedFrom":subQ18}),-1.0]])]})]);}
            var Q1;
            Q1=makeQuery(id+"F5.boolean.opBoolean","SPLIT",FACE,{"disambiguationData":[TD([makeQuery(id+"F5.opExtrude","SWEPT_FACE",FACE,{"disambiguationData":[OSD([sQuery(id+"F4.wireOp",EDGE,"E41")])]})])],"derivedFrom":makeQuery(id+"F3.boolean.opBoolean","COPY",FACE,{"derivedFrom":makeQuery(id+"F3.opExtrude","CAP_FACE",FACE,{"disambiguationData":[OSD([sQuery(id+"F0.wireOp",EDGE,"E25.0"),sQuery(id+"F0.wireOp",EDGE,"E25.1"),sQuery(id+"F0.wireOp",EDGE,"E25.2"),sQuery(id+"F0.wireOp",EDGE,"E25.3"),sQuery(id+"F0.wireOp",EDGE,"E25.4"),sQuery(id+"F0.wireOp",EDGE,"E25.5"),sQuery(id+"F0.wireOp",EDGE,"E25.6"),sQuery(id+"F0.wireOp",EDGE,"E25.7")])],"isStart":false})})});
            extrude(context, id + "F13", {"entities" : qUnion([Q0]), "operationType" : NewBodyOperationType.REMOVE, "endBound" : BoundingType.UP_TO_SURFACE, "endBoundEntityFace" : qUnion([Q1]), "depth" : 25 * mm});
        }
        {
            var Q0;
            Q0=makeQuery(id+"F3.boolean.opBoolean","COPY",EDGE,{"derivedFrom":makeQuery(id+"F3.opExtrude","CAP_EDGE",EDGE,{"disambiguationData":[OSD([sQuery(id+"F0.wireOp",EDGE,"E25.6")])],"isStart":false})});
            var Q1;
            Q1=makeQuery(id+"F8.boolean.opBoolean","INTERSECT",EDGE,{"derivedFrom":[makeQuery(id+"F5.opExtrude","SWEPT_FACE",FACE,{"disambiguationData":[OSD([sQuery(id+"F4.wireOp",EDGE,"E30")])]}),makeQuery(id+"F8.opExtrude","CAP_FACE",FACE,{"disambiguationData":[OSD([sQuery(id+"F7.wireOp",EDGE,"E67")])],"isStart":false})]});
            var Q2;
            Q2=makeQuery(id+"F8.boolean.opBoolean","INTERSECT",EDGE,{"disambiguationData":[OD(1.0)],"derivedFrom":[makeQuery(id+"F5.opExtrude","SWEPT_FACE",FACE,{"disambiguationData":[OSD([sQuery(id+"F4.wireOp",EDGE,"E30")])]}),makeQuery(id+"F8.opExtrude","SWEPT_FACE",FACE,{"disambiguationData":[OSD([sQuery(id+"F7.wireOp",EDGE,"E67")])]})]});
            var Q3;
            {var subQ0=sQuery(id+"F4.wireOp",EDGE,"E30");Q3=makeQuery(id+"F8.boolean.opBoolean","SPLIT",EDGE,{"disambiguationData":[TD([makeQuery(id+"F5.opExtrude","SWEPT_FACE",FACE,{"disambiguationData":[OSD([sQuery(id+"F4.wireOp",EDGE,"E35.filletArc")])]})])],"derivedFrom":makeQuery(id+"F5.opExtrude","CAP_EDGE",EDGE,{"disambiguationData":[OSD([subQ0])],"isStart":false})});}
            var Q4;
            {var subQ0=sQuery(id+"F0.wireOp",EDGE,"E25.7");var subQ1=sQuery(id+"F0.wireOp",EDGE,"E25.1");var subQ2=sQuery(id+"F0.wireOp",EDGE,"E25.6");var subQ3=sQuery(id+"F0.wireOp",EDGE,"E25.5");var subQ4=sQuery(id+"F0.wireOp",EDGE,"E25.4");var subQ5=sQuery(id+"F0.wireOp",EDGE,"E25.0");var subQ6=sQuery(id+"F0.wireOp",EDGE,"E25.2");var subQ7=sQuery(id+"F0.wireOp",EDGE,"E25.3");Q4=makeQuery(id+"F8.boolean.opBoolean","INTERSECT",EDGE,{"derivedFrom":[makeQuery(id+"F5.boolean.opBoolean","SPLIT",FACE,{"disambiguationData":[TD([makeQuery(id+"F2.opExtrude","SWEPT_FACE",FACE,{"disambiguationData":[OSD([subQ5])]})])],"derivedFrom":makeQuery(id+"F3.boolean.opBoolean","COPY",FACE,{"derivedFrom":makeQuery(id+"F3.opExtrude","CAP_FACE",FACE,{"disambiguationData":[OSD([subQ5,subQ1,subQ6,subQ7,subQ4,subQ3,subQ2,subQ0])],"isStart":false})})}),makeQuery(id+"F8.opExtrude","SWEPT_FACE",FACE,{"disambiguationData":[OSD([sQuery(id+"F7.wireOp",EDGE,"E67")])]})]});}
            var Q5;
            Q5=makeQuery(id+"F8.boolean.opBoolean","INTERSECT",EDGE,{"disambiguationData":[OD(0.0)],"derivedFrom":[makeQuery(id+"F5.opExtrude","SWEPT_FACE",FACE,{"disambiguationData":[OSD([sQuery(id+"F4.wireOp",EDGE,"E30")])]}),makeQuery(id+"F8.opExtrude","SWEPT_FACE",FACE,{"disambiguationData":[OSD([sQuery(id+"F7.wireOp",EDGE,"E67")])]})]});
            fillet(context, id + "F14", {"entities" : qUnion([Q0, Q1, Q2, Q3, Q4, Q5]), "radius" : 3 * mm, "tangentPropagation" : true, "allowEdgeOverflow" : false});
        }
        {
            var Q0;
            Q0=makeQuery(id+"F1.opExtrude","CAP_EDGE",EDGE,{"disambiguationData":[OSD([sQuery(id+"F0.wireOp",EDGE,"E1.bottom")])],"isStart":false});
            fillet(context, id + "F15", {"entities" : qUnion([Q0]), "radius" : 2 * mm, "tangentPropagation" : true, "allowEdgeOverflow" : false});
        }
        {
            var Q0;
            {var subQ0=sQuery(id+"F0.wireOp",EDGE,"E21.filletArc");var subQ1=sQuery(id+"F0.wireOp",EDGE,"E7");var subQ2=sQuery(id+"F0.wireOp",EDGE,"E6");var subQ3=sQuery(id+"F0.wireOp",EDGE,"E5");var subQ4=sQuery(id+"F0.wireOp",EDGE,"E4");var subQ5=sQuery(id+"F0.wireOp",EDGE,"E22.filletArc");var subQ6=sQuery(id+"F0.wireOp",EDGE,"E1.bottom");var subQ7=sQuery(id+"F0.wireOp",EDGE,"E1.right");var subQ8=sQuery(id+"F0.wireOp",EDGE,"E1.top");var subQ9=sQuery(id+"F0.wireOp",EDGE,"E1.left");var subQ10=sQuery(id+"F0.wireOp",EDGE,"E23.filletArc");var subQ11=sQuery(id+"F0.wireOp",EDGE,"E24.filletArc");Q0=makeQuery(id+"F2.boolean.opBoolean","SPLIT",FACE,{"disambiguationData":[TD([makeQuery(id+"F1.opExtrude","SWEPT_FACE",FACE,{"disambiguationData":[OSD([subQ6])]})])],"derivedFrom":makeQuery(id+"F1.opExtrude","CAP_FACE",FACE,{"disambiguationData":[OSD([subQ6,subQ8,subQ9,subQ7,subQ4,subQ3,subQ2,subQ1,subQ0,subQ5,subQ10,subQ11])],"isStart":true})});}
            var sketch = newSketch(context, id + "F16", { "sketchPlane" : qUnion([Q0])});
            skCircle(sketch, "E79", {"center": v(0, 104.25) * mm, "radius": 6 * mm});
            skPoint(sketch, "E80", {"position": v(0, 74.25) * mm});
            skLineSegment(sketch, "E81", {"start": v(0, 104.25) * mm, "end": v(0, 74.25) * mm});
            skArc(sketch, "E82", {"start": v(15, 104.25) * mm, "mid": v(0, 119.25) * mm, "end": v(-15, 104.25) * mm});
            skLineSegment(sketch, "E83", {"start": v(-15, 104.25) * mm, "end": v(-15, 92.25) * mm});
            skLineSegment(sketch, "E84", {"start": v(15, 104.25) * mm, "end": v(15, 92.25) * mm});
            skLineSegment(sketch, "E85", {"start": v(15, 92.25) * mm, "end": v(33, 74.25) * mm});
            skLineSegment(sketch, "E86", {"start": v(-15, 92.25) * mm, "end": v(-33, 74.25) * mm});
            skPoint(sketch, "E87.startSnap0", {"position": v(74.25, 0) * mm});
            skArc(sketch, "E88.MirrorCS", {"start": v(15, -104.25) * mm, "mid": v(0, -119.25) * mm, "end": v(-15, -104.25) * mm});
            skLineSegment(sketch, "E89.MirrorCS", {"start": v(-15, -104.25) * mm, "end": v(-15, -92.25) * mm});
            skLineSegment(sketch, "E90.MirrorCS", {"start": v(15, -104.25) * mm, "end": v(15, -92.25) * mm});
            skLineSegment(sketch, "E91.MirrorCS", {"start": v(15, -92.25) * mm, "end": v(33, -74.25) * mm});
            skLineSegment(sketch, "E92.MirrorCS", {"start": v(0, -104.25) * mm, "end": v(0, -74.25) * mm});
            skLineSegment(sketch, "E93.MirrorCS", {"start": v(-15, -92.25) * mm, "end": v(-33, -74.25) * mm});
            skPoint(sketch, "E94.MirrorP", {"position": v(0, -74.25) * mm});
            skCircle(sketch, "E95.MirrorC", {"center": v(0, -104.25) * mm, "radius": 6 * mm});
            skSolve(sketch);
        }
        {
            var Q0;
            Q0=makeQuery(id+"F16.imprint","IMPRINT",FACE,{"disambiguationData":[TD([[makeQuery(id+"F16.imprint","IMPRINT",EDGE,{"derivedFrom":sQuery(id+"F16.wireOp",EDGE,"E79")}),-1.0]])]});
            var Q1;
            Q1=makeQuery(id+"F16.imprint","IMPRINT",FACE,{"disambiguationData":[TD([[makeQuery(id+"F16.imprint","IMPRINT",EDGE,{"derivedFrom":sQuery(id+"F16.wireOp",EDGE,"E88.MirrorCS")}),-1.0]])]});
            extrude(context, id + "F17", {"entities" : qUnion([Q0, Q1]), "depth" : -25 * mm});
        }
    });
